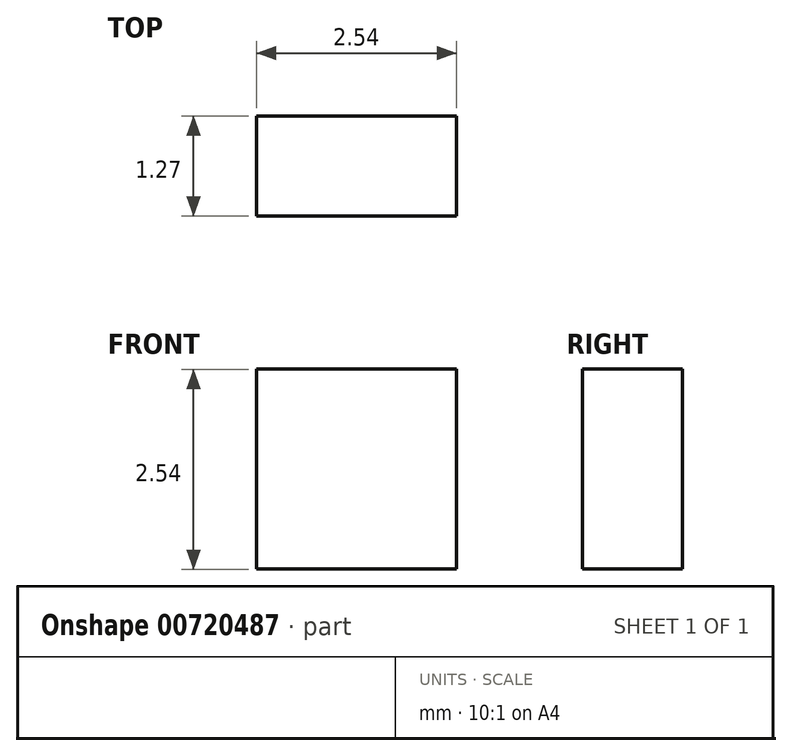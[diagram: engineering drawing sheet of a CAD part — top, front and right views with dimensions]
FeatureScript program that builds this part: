
annotation { "Feature Type Name" : "Feature", "Feature Type Description" : "" }
export const myFeature = defineFeature(function(context is Context, id is Id, definition is map)
    precondition{}
    {
        {
            var Q0;
            Q0=qCreatedBy(makeId("Front.planeOp"),FACE);
            var sketch = newSketch(context, id + "F0", { "sketchPlane" : qUnion([Q0])});
            skLineSegment(sketch, "E0.bottom", {"start": v(-37.81, 25.81) * mm, "end": v(-35.27, 25.81) * mm});
            skLineSegment(sketch, "E0.top", {"start": v(-37.81, 23.27) * mm, "end": v(-35.27, 23.27) * mm});
            skLineSegment(sketch, "E0.left", {"start": v(-37.81, 25.81) * mm, "end": v(-37.81, 23.27) * mm});
            skLineSegment(sketch, "E0.right", {"start": v(-35.27, 25.81) * mm, "end": v(-35.27, 23.27) * mm});
            skSolve(sketch);
        }
        {
            var Q0;
            Q0 = qSketchRegion(id + "F0", true);
            extrude(context, id + "F1", {"entities" : qUnion([Q0]), "depth" : 1.27 * mm, "offsetDistance" : 25.4 * mm});
        }
    });
